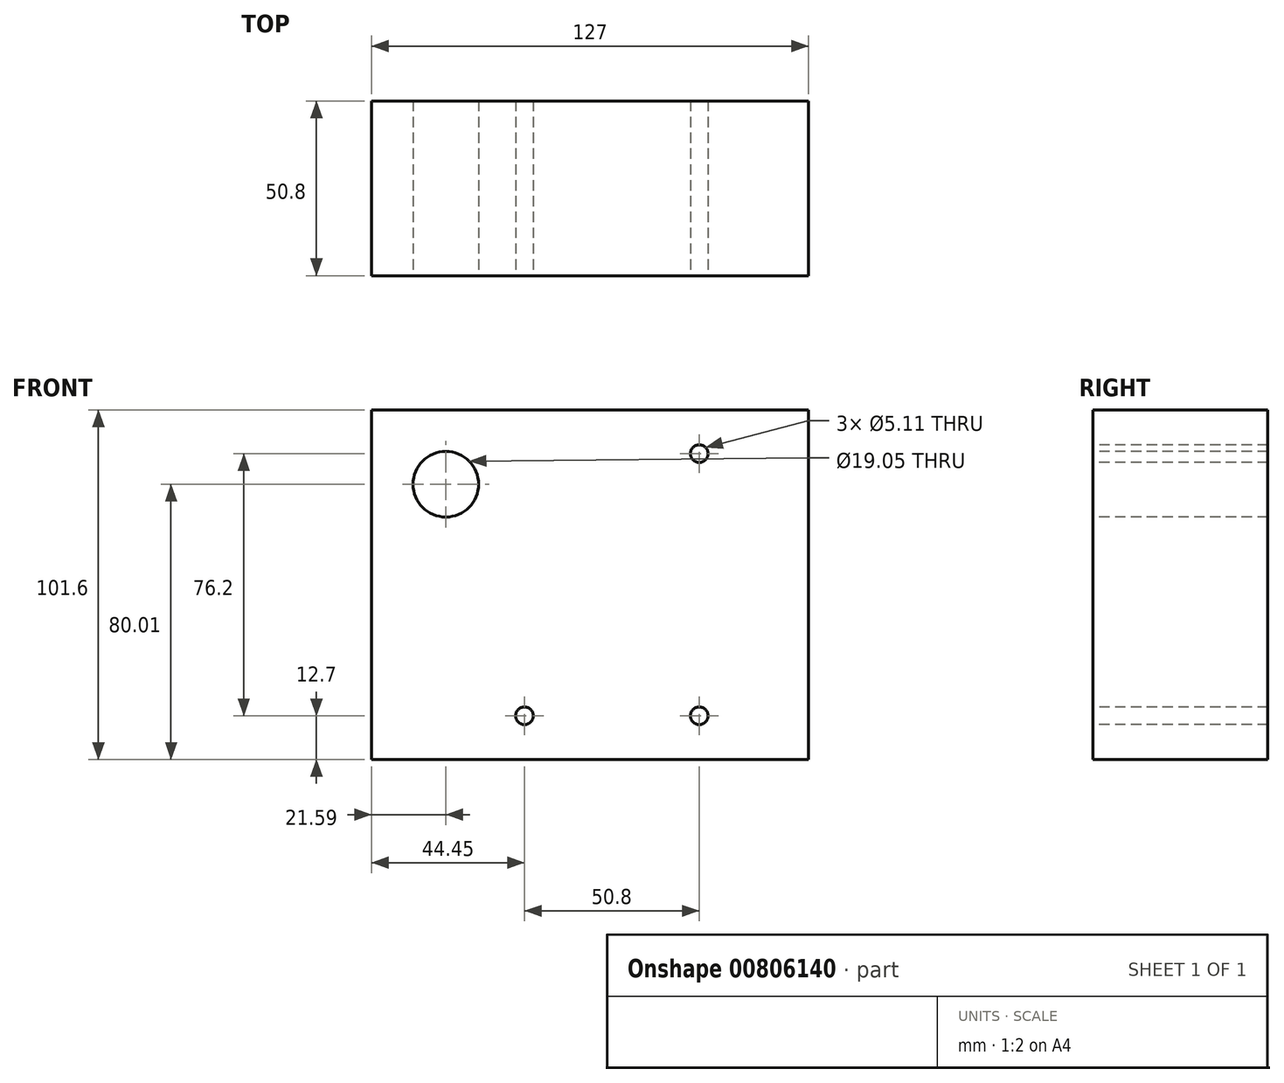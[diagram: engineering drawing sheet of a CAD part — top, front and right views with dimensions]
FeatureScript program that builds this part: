
annotation { "Feature Type Name" : "Feature", "Feature Type Description" : "" }
export const myFeature = defineFeature(function(context is Context, id is Id, definition is map)
    precondition{}
    {
        {
            var Q0;
            Q0=qCreatedBy(makeId("Front.planeOp"),FACE);
            var sketch = newSketch(context, id + "F0", { "sketchPlane" : qUnion([Q0])});
            skLineSegment(sketch, "E0.bottom", {"start": v(-63.5, 50.8) * mm, "end": v(63.5, 50.8) * mm});
            skLineSegment(sketch, "E0.top", {"start": v(-63.5, -50.8) * mm, "end": v(63.5, -50.8) * mm});
            skLineSegment(sketch, "E0.left", {"start": v(-63.5, 50.8) * mm, "end": v(-63.5, -50.8) * mm});
            skLineSegment(sketch, "E0.right", {"start": v(63.5, 50.8) * mm, "end": v(63.5, -50.8) * mm});
            skPoint(sketch, "E0.middle", {"position": v(0, 0) * mm});
            skSolve(sketch);
        }
        {
            var Q0;
            Q0 = qSketchRegion(id + "F0", true);
            extrude(context, id + "F1", {"entities" : qUnion([Q0]), "endBound" : BoundingType.SYMMETRIC, "depth" : 25.4 * mm, "offsetDistance" : 25.4 * mm});
        }
        {
            var Q0;
            Q0=makeQuery(id+"F1.opExtrude","CAP_FACE",FACE,{"disambiguationData":[OSD([sQuery(id+"F0.wireOp",EDGE,"E0.bottom"),sQuery(id+"F0.wireOp",EDGE,"E0.top"),sQuery(id+"F0.wireOp",EDGE,"E0.left"),sQuery(id+"F0.wireOp",EDGE,"E0.right")])],"isStart":false});
            extrude(context, id + "F2", {"entities" : qUnion([Q0]), "operationType" : NewBodyOperationType.ADD, "depth" : 25.4 * mm, "offsetDistance" : 25.4 * mm});
        }
        {
            var Q0;
            Q0=makeQuery(id+"F2.opExtrude","CAP_FACE",FACE,{"disambiguationData":[OSD([sQuery(id+"F0.wireOp",EDGE,"E0.bottom"),sQuery(id+"F0.wireOp",EDGE,"E0.top"),sQuery(id+"F0.wireOp",EDGE,"E0.left"),sQuery(id+"F0.wireOp",EDGE,"E0.right")])],"isStart":false});
            var sketch = newSketch(context, id + "F3", { "sketchPlane" : qUnion([Q0])});
            skCircle(sketch, "E1", {"center": v(-41.9, 29.21) * mm, "radius": 9.53 * mm});
            skSolve(sketch);
        }
        {
            var Q0;
            Q0 = qSketchRegion(id + "F3", true);
            extrude(context, id + "F4", {"entities" : qUnion([Q0]), "operationType" : NewBodyOperationType.REMOVE, "endBound" : BoundingType.THROUGH_ALL, "oppositeDirection" : true, "depth" : 25.4 * mm, "offsetDistance" : 25.4 * mm});
        }
        {
            var Q0;
            Q0=makeQuery(id+"F2.opExtrude","CAP_FACE",FACE,{"disambiguationData":[OSD([sQuery(id+"F0.wireOp",EDGE,"E0.bottom"),sQuery(id+"F0.wireOp",EDGE,"E0.top"),sQuery(id+"F0.wireOp",EDGE,"E0.left"),sQuery(id+"F0.wireOp",EDGE,"E0.right")])],"isStart":false});
            var sketch = newSketch(context, id + "F5", { "sketchPlane" : qUnion([Q0])});
            skPoint(sketch, "E2", {"position": v(31.75, 38.1) * mm});
            skPoint(sketch, "E3", {"position": v(31.75, -38.1) * mm});
            skPoint(sketch, "E4", {"position": v(-19.05, -38.1) * mm});
            skSolve(sketch);
        }
        {
            var Q0;
            Q0=sQuery(id+"F5.wireOp",VERTEX,"E2");
            var Q1;
            Q1=sQuery(id+"F5.wireOp",VERTEX,"E3");
            var Q2;
            Q2=sQuery(id+"F5.wireOp",VERTEX,"E4");
            var Q3;
            Q3=makeQuery(id+"F1.opExtrude","SWEPT_BODY",BODY,{"disambiguationData":[OSD([sQuery(id+"F0.wireOp",EDGE,"E0.bottom"),sQuery(id+"F0.wireOp",EDGE,"E0.top"),sQuery(id+"F0.wireOp",EDGE,"E0.left"),sQuery(id+"F0.wireOp",EDGE,"E0.right")])]});
            hole(context, id + "F6", {"style" : HoleStyle.SIMPLE, "endStyle" : HoleEndStyle.THROUGH, "standardTappedOrClearance" : lookupTablePath({ "standard" : "ANSI", "engagement" : "75%", "pitch" : "20 tpi", "size" : "1/4", "type" : "Tapped" }), "standardBlindInLast" : lookupTablePath({ "standard" : "ANSI", "engagement" : "75%", "pitch" : "20 tpi", "size" : "1/4", "type" : "Tapped" }), "holeDiameter" : 5.1 * mm, "majorDiameter" : 6.35 * mm, "showTappedDepth" : true, "isTappedThrough" : true, "tappedDepth" : 12.7 * mm, "tapClearance" : 3, "locations" : qUnion([Q0, Q1, Q2]), "scope" : qUnion([Q3])});
        }
    });
